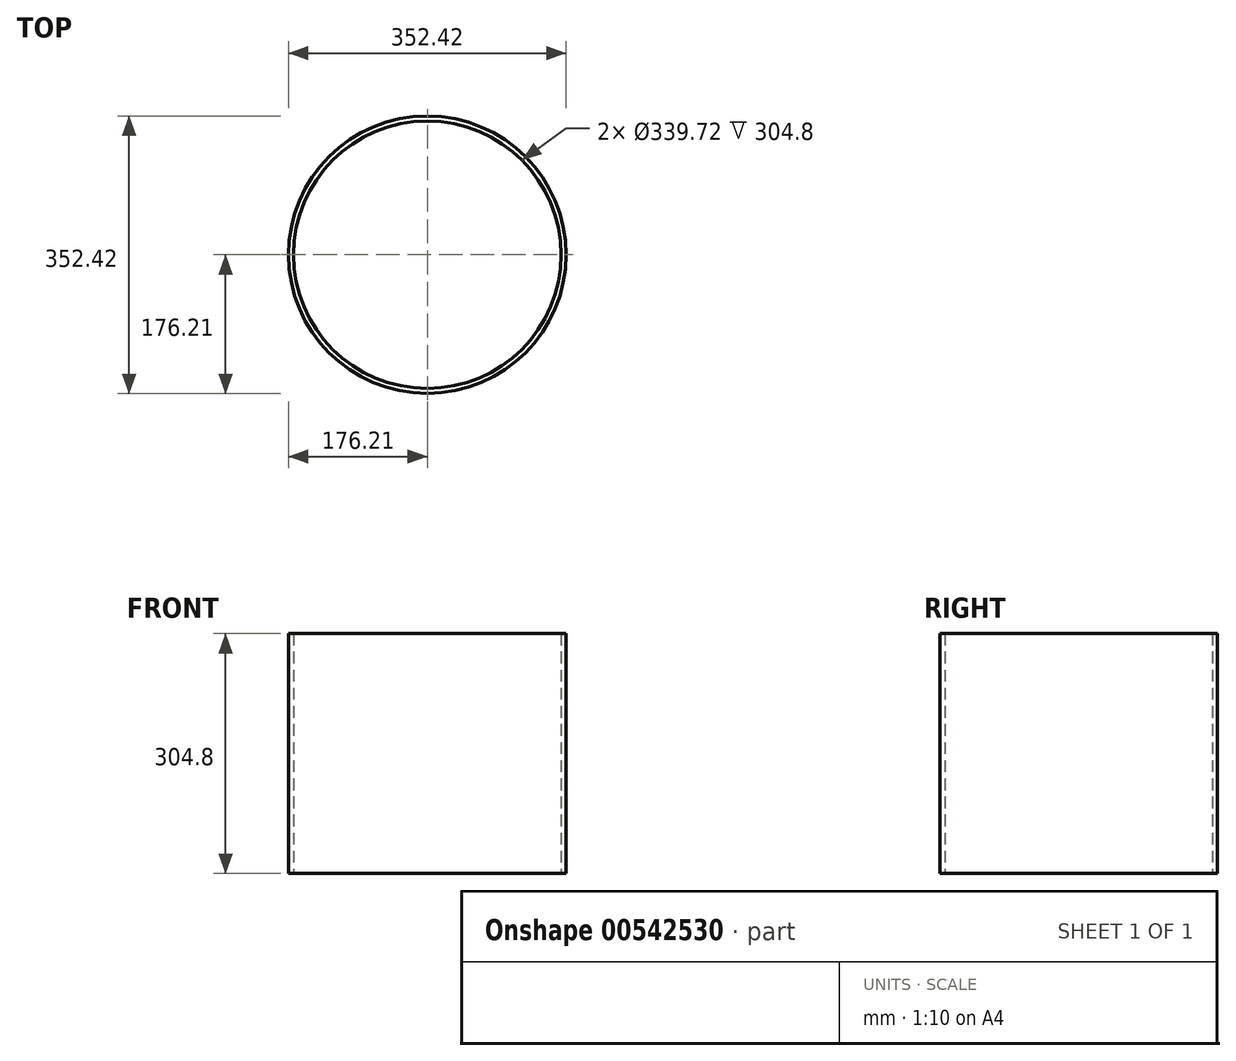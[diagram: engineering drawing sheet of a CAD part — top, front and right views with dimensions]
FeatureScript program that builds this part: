
annotation { "Feature Type Name" : "Feature", "Feature Type Description" : "" }
export const myFeature = defineFeature(function(context is Context, id is Id, definition is map)
    precondition{}
    {
        {
            var Q0;
            Q0=qCreatedBy(makeId("Top.planeOp"),FACE);
            var sketch = newSketch(context, id + "F0", { "sketchPlane" : qUnion([Q0])});
            skCircle(sketch, "E0", {"center": v(0, 0) * mm, "radius": 176.21 * mm});
            skCircle(sketch, "E1.0", {"center": v(0, 0) * mm, "radius": 169.86 * mm});
            skSolve(sketch);
        }
        {
            var Q0;
            Q0 = qSketchRegion(id + "F0", true);
            extrude(context, id + "F1", {"entities" : qUnion([Q0]), "depth" : 304.8 * mm, "offsetDistance" : 25.4 * mm});
        }
    });
